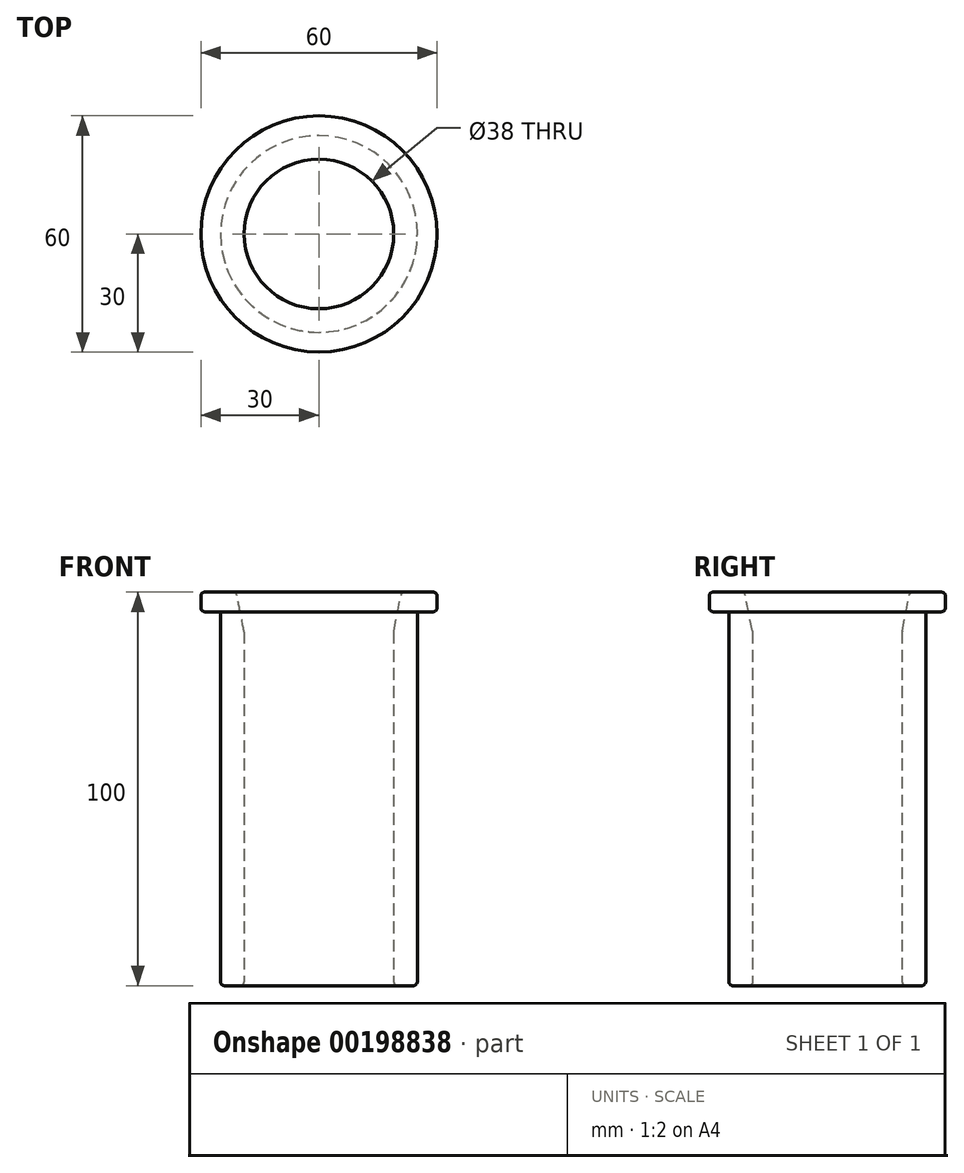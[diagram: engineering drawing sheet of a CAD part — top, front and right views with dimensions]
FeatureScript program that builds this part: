
annotation { "Feature Type Name" : "Feature", "Feature Type Description" : "" }
export const myFeature = defineFeature(function(context is Context, id is Id, definition is map)
    precondition{}
    {
        {
            var Q0;
            Q0=qCreatedBy(makeId("Top.planeOp"),FACE);
            var sketch = newSketch(context, id + "F0", { "sketchPlane" : qUnion([Q0])});
            skCircle(sketch, "E0", {"center": v(0, 0) * mm, "radius": 25 * mm});
            skCircle(sketch, "E1", {"center": v(0, 0) * mm, "radius": 19 * mm});
            skCircle(sketch, "E2", {"center": v(0, 0) * mm, "radius": 30 * mm});
            skLineSegment(sketch, "E3", {"start": v(0, -30) * mm, "end": v(0, 30) * mm, "construction": true});
            skPoint(sketch, "E4", {"position": v(0, 19) * mm});
            skPoint(sketch, "E5", {"position": v(0, 25) * mm});
            skPoint(sketch, "E6", {"position": v(0, 30) * mm});
            skSolve(sketch);
        }
        {
            var Q0;
            Q0=qCreatedBy(makeId("Right.planeOp"),FACE);
            var sketch = newSketch(context, id + "F1", { "sketchPlane" : qUnion([Q0])});
            skLineSegment(sketch, "E7.left", {"start": v(-19, -95) * mm, "end": v(-19, 0) * mm});
            skLineSegment(sketch, "E7.right", {"start": v(19, -95) * mm, "end": v(19, 0) * mm});
            skLineSegment(sketch, "E8.top", {"start": v(-25, -95) * mm, "end": v(25, -95) * mm});
            skLineSegment(sketch, "E8.left", {"start": v(-25, 0) * mm, "end": v(-25, -95) * mm});
            skLineSegment(sketch, "E8.right", {"start": v(25, 0) * mm, "end": v(25, -95) * mm});
            skLineSegment(sketch, "E9.bottom", {"start": v(30, 5) * mm, "end": v(-30, 5) * mm});
            skLineSegment(sketch, "E9.top", {"start": v(30, 0) * mm, "end": v(-30, 0) * mm});
            skLineSegment(sketch, "E9.left", {"start": v(30, 5) * mm, "end": v(30, 0) * mm});
            skLineSegment(sketch, "E9.right", {"start": v(-30, 5) * mm, "end": v(-30, 0) * mm});
            skLineSegment(sketch, "E10", {"start": v(0, 5) * mm, "end": v(0, -95) * mm, "construction": true});
            skSolve(sketch);
        }
        {
            var Q0;
            Q0=makeQuery(id+"F0.imprint","IMPRINT",FACE,{"disambiguationData":[TD([[makeQuery(id+"F0.imprint","IMPRINT",EDGE,{"derivedFrom":sQuery(id+"F0.wireOp",EDGE,"E0")}),1.0]])]});
            var Q1;
            Q1=makeQuery(id+"F0.imprint","IMPRINT",FACE,{"disambiguationData":[TD([[makeQuery(id+"F0.imprint","IMPRINT",EDGE,{"derivedFrom":sQuery(id+"F0.wireOp",EDGE,"E0")}),-1.0]])]});
            var Q2;
            Q2=sQuery(id+"F1.wireOp",VERTEX,"E9.bottom.end");
            extrude(context, id + "F2", {"entities" : qUnion([Q0, Q1]), "endBound" : BoundingType.UP_TO_VERTEX, "endBoundEntityVertex" : qUnion([Q2]), "depth" : 25 * mm});
        }
        {
            var Q0;
            Q0=makeQuery(id+"F0.imprint","IMPRINT",FACE,{"disambiguationData":[TD([[makeQuery(id+"F0.imprint","IMPRINT",EDGE,{"derivedFrom":sQuery(id+"F0.wireOp",EDGE,"E0")}),1.0]])]});
            var Q1;
            Q1=sQuery(id+"F1.wireOp",VERTEX,"E7.left.start");
            extrude(context, id + "F3", {"entities" : qUnion([Q0]), "operationType" : NewBodyOperationType.ADD, "endBound" : BoundingType.UP_TO_VERTEX, "oppositeDirection" : true, "endBoundEntityVertex" : qUnion([Q1]), "depth" : 25 * mm});
        }
        {
            var Q0;
            Q0=makeQuery(id+"F2.opExtrude","CAP_EDGE",EDGE,{"disambiguationData":[OSD([sQuery(id+"F0.wireOp",EDGE,"E1")])],"isStart":false});
            chamfer(context, id + "F4", {"entities" : qUnion([Q0]), "chamferType" : ChamferType.TWO_OFFSETS, "width1" : 2 * mm, "oppositeDirection" : true, "width2" : 10 * mm, "tangentPropagation" : true});
        }
        {
            var Q0;
            Q0=makeQuery(id+"F2.opExtrude","CAP_EDGE",EDGE,{"disambiguationData":[OSD([sQuery(id+"F0.wireOp",EDGE,"E2")])],"isStart":false});
            var Q1;
            Q1=makeQuery(id+"F2.opExtrude","CAP_EDGE",EDGE,{"disambiguationData":[OSD([sQuery(id+"F0.wireOp",EDGE,"E2")])],"isStart":true});
            var Q2;
            Q2=makeQuery(id+"F3.opExtrude","CAP_EDGE",EDGE,{"disambiguationData":[OSD([sQuery(id+"F0.wireOp",EDGE,"E0")])],"isStart":false});
            var Q3;
            Q3=makeQuery(id+"F3.opExtrude","CAP_EDGE",EDGE,{"disambiguationData":[OSD([sQuery(id+"F0.wireOp",EDGE,"E1")])],"isStart":false});
            var Q4;
            {var subQ0=sQuery(id+"F0.wireOp",EDGE,"E1");Q4=makeQuery(id+"F4.opChamfer","BLEND_EDGE",EDGE,{"blendedFrom":[makeQuery(id+"F2.opExtrude","CAP_EDGE",EDGE,{"disambiguationData":[OSD([subQ0])],"isStart":false}),makeQuery(id+"F2.opExtrude","CAP_FACE",FACE,{"disambiguationData":[OSD([subQ0,sQuery(id+"F0.wireOp",EDGE,"E2")])],"isStart":false})],"blendedInto":[makeQuery(id+"F2.opExtrude","CAP_FACE",FACE,{"disambiguationData":[OSD([subQ0,sQuery(id+"F0.wireOp",EDGE,"E2")])],"isStart":false})]});}
            var Q5;
            {var subQ0=sQuery(id+"F0.wireOp",EDGE,"E1");Q5=makeQuery(id+"F4.opChamfer","BLEND_EDGE",EDGE,{"blendedFrom":[makeQuery(id+"F2.opExtrude","CAP_EDGE",EDGE,{"disambiguationData":[OSD([subQ0])],"isStart":false}),makeQuery(id+"F3.boolean.opBoolean","MERGE",FACE,{"derivedFrom":[makeQuery(id+"F2.opExtrude","SWEPT_FACE",FACE,{"disambiguationData":[OSD([subQ0])]}),makeQuery(id+"F3.opExtrude","SWEPT_FACE",FACE,{"disambiguationData":[OSD([subQ0])]})]})],"blendedInto":[makeQuery(id+"F3.boolean.opBoolean","MERGE",FACE,{"derivedFrom":[makeQuery(id+"F2.opExtrude","SWEPT_FACE",FACE,{"disambiguationData":[OSD([subQ0])]}),makeQuery(id+"F3.opExtrude","SWEPT_FACE",FACE,{"disambiguationData":[OSD([subQ0])]})]})]});}
            fillet(context, id + "F5", {"entities" : qUnion([Q0, Q1, Q2, Q3, Q4, Q5]), "radius" : 1 * mm, "tangentPropagation" : true, "allowEdgeOverflow" : false});
        }
    });
